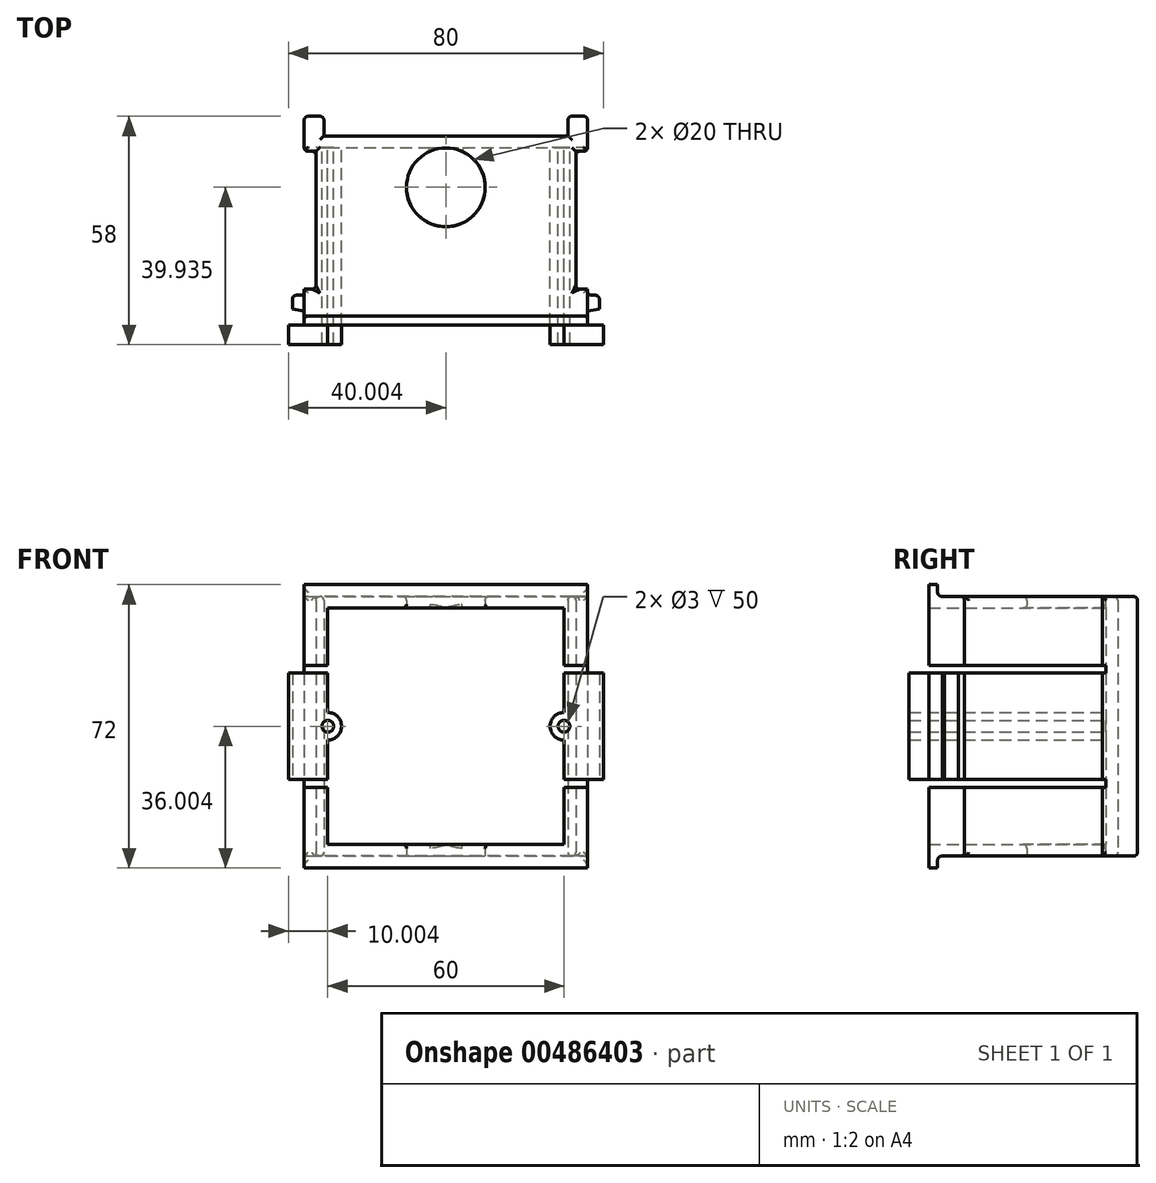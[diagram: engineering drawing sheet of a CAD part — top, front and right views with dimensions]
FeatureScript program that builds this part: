
annotation { "Feature Type Name" : "Feature", "Feature Type Description" : "" }
export const myFeature = defineFeature(function(context is Context, id is Id, definition is map)
    precondition{}
    {
        {
            var Q0;
            Q0=qCreatedBy(makeId("Front.planeOp"),FACE);
            var sketch = newSketch(context, id + "F0", { "sketchPlane" : qUnion([Q0])});
            skLineSegment(sketch, "E0.bottom", {"start": v(-38.09, 40.21) * mm, "end": v(21.91, 40.21) * mm});
            skLineSegment(sketch, "E0.top", {"start": v(-38.09, -19.79) * mm, "end": v(21.91, -19.79) * mm});
            skLineSegment(sketch, "E0.left", {"start": v(-38.09, 40.21) * mm, "end": v(-38.09, 13.71) * mm});
            skLineSegment(sketch, "E0.right", {"start": v(21.91, 40.21) * mm, "end": v(21.91, 13.71) * mm});
            skCircle(sketch, "E1", {"center": v(-38.09, 10.21) * mm, "radius": 1.5 * mm});
            skCircle(sketch, "E2", {"center": v(21.91, 10.21) * mm, "radius": 1.5 * mm});
            skArc(sketch, "E3", {"start": v(-38.09, 6.71) * mm, "mid": v(-34.59, 10.21) * mm, "end": v(-38.09, 13.71) * mm});
            skArc(sketch, "E4", {"start": v(21.91, 13.71) * mm, "mid": v(18.41, 10.21) * mm, "end": v(21.91, 6.71) * mm});
            skLineSegment(sketch, "E5.trimOffspring", {"start": v(-38.09, 6.71) * mm, "end": v(-38.09, -19.79) * mm});
            skLineSegment(sketch, "E6.trimOffspring", {"start": v(21.91, 6.71) * mm, "end": v(21.91, -19.79) * mm});
            skLineSegment(sketch, "E7.bottom", {"start": v(27.91, 46.21) * mm, "end": v(-44.09, 46.21) * mm});
            skLineSegment(sketch, "E7.top", {"start": v(27.91, -25.79) * mm, "end": v(-44.09, -25.79) * mm});
            skLineSegment(sketch, "E7.left", {"start": v(27.91, 46.21) * mm, "end": v(27.91, -25.79) * mm});
            skLineSegment(sketch, "E7.right", {"start": v(-44.09, 46.21) * mm, "end": v(-44.09, -25.79) * mm});
            skPoint(sketch, "E7.middle", {"position": v(-8.09, 10.21) * mm});
            skPoint(sketch, "E7.middle.positionSnap0", {"position": v(18.41, 10.21) * mm});
            skPoint(sketch, "E7.middle.positionSnap1", {"position": v(-8.09, 40.21) * mm});
            skPoint(sketch, "E7.centerSnap0", {"position": v(18.41, 10.21) * mm});
            skPoint(sketch, "E7.centerSnap1", {"position": v(-8.09, 40.21) * mm});
            skSolve(sketch);
        }
        {
            var Q0;
            Q0 = qSketchRegion(id + "F0", true);
            var Q1;
            Q1 = qConstructionFilter(qBodyType(qCreatedBy(id + "F0" ,EDGE), BodyType.WIRE), ConstructionObject.NO);
            extrude(context, id + "F1", {"entities" : qUnion([Q0]), "surfaceEntities" : qUnion([Q1]), "depth" : 45 * mm});
        }
        {
            var Q0;
            Q0=makeQuery(id+"F1.opExtrude","CAP_FACE",FACE,{"disambiguationData":[OSD([sQuery(id+"F0.wireOp",EDGE,"E0.bottom"),sQuery(id+"F0.wireOp",EDGE,"E0.top"),sQuery(id+"F0.wireOp",EDGE,"E0.left"),sQuery(id+"F0.wireOp",EDGE,"E0.right"),sQuery(id+"F0.wireOp",EDGE,"E1"),sQuery(id+"F0.wireOp",EDGE,"E2"),sQuery(id+"F0.wireOp",EDGE,"E3"),sQuery(id+"F0.wireOp",EDGE,"E4"),sQuery(id+"F0.wireOp",EDGE,"E5.trimOffspring"),sQuery(id+"F0.wireOp",EDGE,"E6.trimOffspring"),sQuery(id+"F0.wireOp",EDGE,"E7.bottom"),sQuery(id+"F0.wireOp",EDGE,"E7.top"),sQuery(id+"F0.wireOp",EDGE,"E7.left"),sQuery(id+"F0.wireOp",EDGE,"E7.right")])],"isStart":true});
            var sketch = newSketch(context, id + "F2", { "sketchPlane" : qUnion([Q0])});
            skLineSegment(sketch, "E8.bottom", {"start": v(-27.91, 46.21) * mm, "end": v(44.09, 46.21) * mm});
            skLineSegment(sketch, "E8.top", {"start": v(-27.91, -25.79) * mm, "end": v(44.09, -25.79) * mm});
            skLineSegment(sketch, "E8.left", {"start": v(-27.91, 46.21) * mm, "end": v(-27.91, -25.79) * mm});
            skLineSegment(sketch, "E8.right", {"start": v(44.09, 46.21) * mm, "end": v(44.09, -25.79) * mm});
            skSolve(sketch);
        }
        {
            var Q0;
            Q0 = qSketchRegion(id + "F2", true);
            extrude(context, id + "F3", {"entities" : qUnion([Q0]), "operationType" : NewBodyOperationType.ADD, "depth" : 3 * mm});
        }
        {
            var Q0;
            Q0=makeQuery(id+"F3.opExtrude","CAP_FACE",FACE,{"disambiguationData":[OSD([sQuery(id+"F2.wireOp",EDGE,"E8.bottom"),sQuery(id+"F2.wireOp",EDGE,"E8.top"),sQuery(id+"F2.wireOp",EDGE,"E8.left"),sQuery(id+"F2.wireOp",EDGE,"E8.right")])],"isStart":false});
            var sketch = newSketch(context, id + "F4", { "sketchPlane" : qUnion([Q0])});
            skLineSegment(sketch, "E9.bottom", {"start": v(44.09, 46.21) * mm, "end": v(39.09, 46.21) * mm});
            skLineSegment(sketch, "E9.top", {"start": v(44.09, -25.79) * mm, "end": v(39.09, -25.79) * mm});
            skLineSegment(sketch, "E9.left", {"start": v(44.09, 46.21) * mm, "end": v(44.09, -25.79) * mm});
            skLineSegment(sketch, "E9.right", {"start": v(39.09, 46.21) * mm, "end": v(39.09, -25.79) * mm});
            skLineSegment(sketch, "E10.bottom", {"start": v(-27.91, 46.21) * mm, "end": v(-22.91, 46.21) * mm});
            skLineSegment(sketch, "E10.top", {"start": v(-27.91, -25.79) * mm, "end": v(-22.91, -25.79) * mm});
            skLineSegment(sketch, "E10.left", {"start": v(-27.91, 46.21) * mm, "end": v(-27.91, -25.79) * mm});
            skLineSegment(sketch, "E10.right", {"start": v(-22.91, 46.21) * mm, "end": v(-22.91, -25.79) * mm});
            skSolve(sketch);
        }
        {
            var Q0;
            Q0 = qSketchRegion(id + "F4", true);
            extrude(context, id + "F5", {"entities" : qUnion([Q0]), "operationType" : NewBodyOperationType.ADD, "depth" : 5 * mm});
        }
        {
            var Q0;
            Q0=makeQuery(id+"F1.opExtrude","CAP_FACE",FACE,{"disambiguationData":[OSD([sQuery(id+"F0.wireOp",EDGE,"E0.bottom"),sQuery(id+"F0.wireOp",EDGE,"E0.top"),sQuery(id+"F0.wireOp",EDGE,"E0.left"),sQuery(id+"F0.wireOp",EDGE,"E0.right"),sQuery(id+"F0.wireOp",EDGE,"E1"),sQuery(id+"F0.wireOp",EDGE,"E2"),sQuery(id+"F0.wireOp",EDGE,"E3"),sQuery(id+"F0.wireOp",EDGE,"E4"),sQuery(id+"F0.wireOp",EDGE,"E5.trimOffspring"),sQuery(id+"F0.wireOp",EDGE,"E6.trimOffspring"),sQuery(id+"F0.wireOp",EDGE,"E7.bottom"),sQuery(id+"F0.wireOp",EDGE,"E7.top"),sQuery(id+"F0.wireOp",EDGE,"E7.left"),sQuery(id+"F0.wireOp",EDGE,"E7.right")])],"isStart":false});
            var sketch = newSketch(context, id + "F6", { "sketchPlane" : qUnion([Q0])});
            skLineSegment(sketch, "E11.bottom", {"start": v(-38.09, 23.71) * mm, "end": v(-48.09, 23.71) * mm});
            skLineSegment(sketch, "E11.top", {"start": v(-38.09, -3.29) * mm, "end": v(-48.09, -3.29) * mm});
            skLineSegment(sketch, "E11.left", {"start": v(-38.09, 23.71) * mm, "end": v(-38.09, 13.71) * mm});
            skLineSegment(sketch, "E11.right", {"start": v(-48.09, 23.71) * mm, "end": v(-48.09, -3.29) * mm});
            skArc(sketch, "E12", {"start": v(-38.09, 6.71) * mm, "mid": v(-34.59, 10.21) * mm, "end": v(-38.09, 13.71) * mm});
            skCircle(sketch, "E13", {"center": v(-38.09, 10.21) * mm, "radius": 1.5 * mm});
            skLineSegment(sketch, "E14.trimOffspring", {"start": v(-38.09, 6.71) * mm, "end": v(-38.09, -3.29) * mm});
            skLineSegment(sketch, "E15", {"start": v(-8.09, 40.21) * mm, "end": v(-8.09, -19.79) * mm, "construction": true});
            skLineSegment(sketch, "E16.MirrorCS", {"start": v(21.91, 23.71) * mm, "end": v(31.91, 23.71) * mm});
            skLineSegment(sketch, "E17.MirrorCS", {"start": v(21.91, -3.29) * mm, "end": v(31.91, -3.29) * mm});
            skLineSegment(sketch, "E18.MirrorCS", {"start": v(21.91, 23.71) * mm, "end": v(21.91, 13.71) * mm});
            skLineSegment(sketch, "E19.MirrorCS", {"start": v(21.91, 6.71) * mm, "end": v(21.91, -3.29) * mm});
            skLineSegment(sketch, "E20.MirrorCS", {"start": v(31.91, 23.71) * mm, "end": v(31.91, -3.29) * mm});
            skArc(sketch, "E21.MirrorCS", {"start": v(21.91, 6.71) * mm, "mid": v(18.41, 10.21) * mm, "end": v(21.91, 13.71) * mm});
            skCircle(sketch, "E22.MirrorC", {"center": v(21.91, 10.21) * mm, "radius": 1.5 * mm});
            skSolve(sketch);
        }
        {
            var Q0;
            Q0 = qSketchRegion(id + "F6", true);
            extrude(context, id + "F7", {"entities" : qUnion([Q0]), "operationType" : NewBodyOperationType.ADD, "depth" : 5 * mm});
        }
        {
            var Q0;
            Q0=makeQuery(id+"F5.boolean.opBoolean","MERGE",FACE,{"derivedFrom":[makeQuery(id+"F3.boolean.opBoolean","MERGE",FACE,{"derivedFrom":[makeQuery(id+"F1.opExtrude","SWEPT_FACE",FACE,{"disambiguationData":[OSD([sQuery(id+"F0.wireOp",EDGE,"E7.right")])]}),makeQuery(id+"F3.opExtrude","SWEPT_FACE",FACE,{"disambiguationData":[OSD([sQuery(id+"F2.wireOp",EDGE,"E8.right")])]})]}),makeQuery(id+"F5.opExtrude","SWEPT_FACE",FACE,{"disambiguationData":[OSD([sQuery(id+"F4.wireOp",EDGE,"E9.left")])]})]});
            var sketch = newSketch(context, id + "F8", { "sketchPlane" : qUnion([Q0])});
            skLineSegment(sketch, "E23.bottom", {"start": v(45, 23.71) * mm, "end": v(0, 23.71) * mm});
            skLineSegment(sketch, "E23.top", {"start": v(45, 25.71) * mm, "end": v(0, 25.71) * mm});
            skLineSegment(sketch, "E23.left", {"start": v(45, 23.71) * mm, "end": v(45, 25.71) * mm});
            skLineSegment(sketch, "E23.right", {"start": v(0, 23.71) * mm, "end": v(0, 25.71) * mm});
            skLineSegment(sketch, "E24.bottom", {"start": v(45, -3.29) * mm, "end": v(0, -3.29) * mm});
            skLineSegment(sketch, "E24.top", {"start": v(45, -5.29) * mm, "end": v(0, -5.29) * mm});
            skLineSegment(sketch, "E24.left", {"start": v(45, -3.29) * mm, "end": v(45, -5.29) * mm});
            skLineSegment(sketch, "E24.right", {"start": v(0, -3.29) * mm, "end": v(0, -5.29) * mm});
            skSolve(sketch);
        }
        {
            var Q0;
            Q0 = qSketchRegion(id + "F8", true);
            extrude(context, id + "F9", {"entities" : qUnion([Q0]), "operationType" : NewBodyOperationType.REMOVE, "oppositeDirection" : true, "depth" : 100 * mm});
        }
        {
            var Q0;
            Q0=makeQuery(id+"F9.boolean.opBoolean","MERGE",FACE,{"derivedFrom":[makeQuery(id+"F7.opExtrude","SWEPT_FACE",FACE,{"disambiguationData":[OSD([sQuery(id+"F6.wireOp",EDGE,"E11.top")])]}),makeQuery(id+"F9.opExtrude","SWEPT_FACE",FACE,{"disambiguationData":[OSD([sQuery(id+"F8.wireOp",EDGE,"E24.bottom")])]})]});
            var sketch = newSketch(context, id + "F10", { "sketchPlane" : qUnion([Q0])});
            skLineSegment(sketch, "E25.top", {"start": v(-44.09, 37.5) * mm, "end": v(-47.09, 37.5) * mm});
            skLineSegment(sketch, "E25.left", {"start": v(-44.09, 41.5) * mm, "end": v(-44.09, 37.5) * mm});
            skLineSegment(sketch, "E25.right", {"start": v(-47.09, 40.97) * mm, "end": v(-47.09, 37.5) * mm});
            skLineSegment(sketch, "E26", {"start": v(-44.09, 41.5) * mm, "end": v(-47.09, 40.97) * mm});
            skLineSegment(sketch, "E27", {"start": v(-8.09, 43.31) * mm, "end": v(-8.09, 15.36) * mm, "construction": true});
            skLineSegment(sketch, "E28.MirrorCS", {"start": v(27.91, 41.5) * mm, "end": v(30.91, 40.97) * mm});
            skLineSegment(sketch, "E29.MirrorCS", {"start": v(27.91, 37.5) * mm, "end": v(30.91, 37.5) * mm});
            skLineSegment(sketch, "E30.MirrorCS", {"start": v(30.91, 40.97) * mm, "end": v(30.91, 37.5) * mm});
            skLineSegment(sketch, "E31.MirrorCS", {"start": v(27.91, 41.5) * mm, "end": v(27.91, 37.5) * mm});
            skSolve(sketch);
        }
        {
            var Q0;
            Q0 = qSketchRegion(id + "F10", true);
            extrude(context, id + "F11", {"entities" : qUnion([Q0]), "operationType" : NewBodyOperationType.ADD, "oppositeDirection" : true, "depth" : 27 * mm});
        }
        {
            var Q0;
            {var subQ0=sQuery(id+"F4.wireOp",EDGE,"E10.left");var subQ3=sQuery(id+"F0.wireOp",EDGE,"E7.left");var subQ5=sQuery(id+"F0.wireOp",EDGE,"E7.bottom");var subQ15=sQuery(id+"F2.wireOp",EDGE,"E8.left");var subQ18=makeQuery(id+"F1.opExtrude","SWEPT_FACE",FACE,{"disambiguationData":[OSD([subQ3])]});var subQ19=makeQuery(id+"F3.opExtrude","SWEPT_FACE",FACE,{"disambiguationData":[OSD([subQ15])]});var subQ20=makeQuery(id+"F5.opExtrude","SWEPT_FACE",FACE,{"disambiguationData":[OSD([subQ0])]});Q0=makeQuery(id+"F11.boolean.opBoolean","SPLIT",FACE,{"disambiguationData":[TD([makeQuery(id+"F1.opExtrude","SWEPT_FACE",FACE,{"disambiguationData":[OSD([subQ5])]})])],"derivedFrom":makeQuery(id+"F5.boolean.opBoolean","MERGE",FACE,{"derivedFrom":[makeQuery(id+"F3.boolean.opBoolean","MERGE",FACE,{"derivedFrom":[subQ18,subQ19]}),subQ20]})});}
            var sketch = newSketch(context, id + "F12", { "sketchPlane" : qUnion([Q0])});
            skLineSegment(sketch, "E32", {"start": v(8, 10.21) * mm, "end": v(-53.5, 10.21) * mm, "construction": true});
            skLineSegment(sketch, "E33.bottom", {"start": v(-42.74, 46.21) * mm, "end": v(8, 46.21) * mm});
            skLineSegment(sketch, "E33.top", {"start": v(-42.74, 43.21) * mm, "end": v(8, 43.21) * mm});
            skLineSegment(sketch, "E33.left", {"start": v(-42.74, 46.21) * mm, "end": v(-42.74, 43.21) * mm});
            skLineSegment(sketch, "E33.right", {"start": v(8, 46.21) * mm, "end": v(8, 43.21) * mm});
            skLineSegment(sketch, "E34.MirrorCS", {"start": v(8, -25.79) * mm, "end": v(8, -22.79) * mm});
            skLineSegment(sketch, "E35.MirrorCS", {"start": v(-42.74, -22.79) * mm, "end": v(8, -22.79) * mm});
            skLineSegment(sketch, "E36.MirrorCS", {"start": v(-42.74, -25.79) * mm, "end": v(-42.74, -22.79) * mm});
            skLineSegment(sketch, "E37.MirrorCS", {"start": v(-42.74, -25.79) * mm, "end": v(8, -25.79) * mm});
            skSolve(sketch);
        }
        {
            var Q0;
            Q0 = qSketchRegion(id + "F12", true);
            extrude(context, id + "F13", {"entities" : qUnion([Q0]), "operationType" : NewBodyOperationType.REMOVE, "endBound" : BoundingType.UP_TO_NEXT, "oppositeDirection" : true, "depth" : 25 * mm});
        }
        {
            var Q0;
            Q0=makeQuery(id+"F13.boolean.opBoolean","COPY",FACE,{"derivedFrom":makeQuery(id+"F13.opExtrude","SWEPT_FACE",FACE,{"disambiguationData":[OSD([sQuery(id+"F12.wireOp",EDGE,"E35.MirrorCS")])]})});
            var sketch = newSketch(context, id + "F14", { "sketchPlane" : qUnion([Q0])});
            skLineSegment(sketch, "E38", {"start": v(-8.09, -3) * mm, "end": v(-8.09, 55.12) * mm, "construction": true});
            skLineSegment(sketch, "E39.bottom", {"start": v(27.91, 35.92) * mm, "end": v(24.91, 35.92) * mm});
            skLineSegment(sketch, "E39.top", {"start": v(27.91, 0.92) * mm, "end": v(24.91, 0.92) * mm});
            skLineSegment(sketch, "E39.left", {"start": v(27.91, 35.92) * mm, "end": v(27.91, 0.92) * mm});
            skLineSegment(sketch, "E39.right", {"start": v(24.91, 35.92) * mm, "end": v(24.91, 0.92) * mm});
            skLineSegment(sketch, "E40.MirrorCS", {"start": v(-44.09, 0.92) * mm, "end": v(-41.09, 0.92) * mm});
            skLineSegment(sketch, "E41.MirrorCS", {"start": v(-44.09, 35.92) * mm, "end": v(-41.09, 35.92) * mm});
            skLineSegment(sketch, "E42.MirrorCS", {"start": v(-41.09, 35.92) * mm, "end": v(-41.09, 0.92) * mm});
            skLineSegment(sketch, "E43.MirrorCS", {"start": v(-44.09, 35.92) * mm, "end": v(-44.09, 0.92) * mm});
            skSolve(sketch);
        }
        {
            var Q0;
            Q0 = qSketchRegion(id + "F14", true);
            extrude(context, id + "F15", {"entities" : qUnion([Q0]), "operationType" : NewBodyOperationType.REMOVE, "endBound" : BoundingType.THROUGH_ALL, "oppositeDirection" : true, "depth" : 25 * mm});
        }
        {
            var Q0;
            Q0=makeQuery(id+"F13.boolean.opBoolean","COPY",FACE,{"derivedFrom":makeQuery(id+"F13.opExtrude","SWEPT_FACE",FACE,{"disambiguationData":[OSD([sQuery(id+"F12.wireOp",EDGE,"E35.MirrorCS")])]})});
            var Q1;
            Q1=makeQuery(id+"F13.boolean.opBoolean","COPY",FACE,{"derivedFrom":makeQuery(id+"F13.opExtrude","SWEPT_FACE",FACE,{"disambiguationData":[OSD([sQuery(id+"F12.wireOp",EDGE,"E33.top")])]})});
            fillet(context, id + "F16", {"entities" : qUnion([Q0, Q1]), "radius" : 1 * mm, "tangentPropagation" : true, "allowEdgeOverflow" : false});
        }
        {
            var Q0;
            {var subQ0=sQuery(id+"F14.wireOp",EDGE,"E39.bottom");var subQ5=sQuery(id+"F14.wireOp",EDGE,"E39.right");Q0=makeQuery(id+"F15.boolean.opBoolean","COPY",EDGE,{"disambiguationData":[TD([makeQuery(id+"F7.opExtrude","SWEPT_FACE",FACE,{"disambiguationData":[OSD([sQuery(id+"F6.wireOp",EDGE,"E16.MirrorCS")])]})])],"derivedFrom":makeQuery(id+"F15.opExtrude","SWEPT_EDGE",EDGE,{"disambiguationData":[OSD([subQ0,subQ5])]})});}
            var Q1;
            Q1=makeQuery(id+"F11.opExtrude","SWEPT_EDGE",EDGE,{"disambiguationData":[OSD([sQuery(id+"F10.wireOp",EDGE,"E29.MirrorCS"),sQuery(id+"F10.wireOp",EDGE,"E31.MirrorCS")])]});
            var Q2;
            Q2=makeQuery(id+"F11.opExtrude","SWEPT_EDGE",EDGE,{"disambiguationData":[OSD([sQuery(id+"F10.wireOp",EDGE,"E29.MirrorCS"),sQuery(id+"F10.wireOp",EDGE,"E30.MirrorCS")])]});
            var Q3;
            Q3=makeQuery(id+"F11.opExtrude","SWEPT_EDGE",EDGE,{"disambiguationData":[OSD([sQuery(id+"F10.wireOp",EDGE,"E25.top"),sQuery(id+"F10.wireOp",EDGE,"E25.right")])]});
            var Q4;
            {var subQ4=sQuery(id+"F4.wireOp",EDGE,"E9.left");var subQ5=sQuery(id+"F2.wireOp",EDGE,"E8.right");var subQ6=sQuery(id+"F0.wireOp",EDGE,"E7.right");var subQ7=sQuery(id+"F14.wireOp",EDGE,"E41.MirrorCS");Q4=makeQuery(id+"F15.boolean.opBoolean","COPY",EDGE,{"disambiguationData":[TD([makeQuery(id+"F7.opExtrude","SWEPT_FACE",FACE,{"disambiguationData":[OSD([sQuery(id+"F6.wireOp",EDGE,"E11.bottom")])]})])],"derivedFrom":makeQuery(id+"F15.opExtrude","SWEPT_EDGE",EDGE,{"disambiguationData":[OSD([subQ6,subQ5,subQ4,sQuery(id+"F12.wireOp",EDGE,"E35.MirrorCS"),subQ7,sQuery(id+"F14.wireOp",EDGE,"E43.MirrorCS")])]})});}
            var Q5;
            {var subQ4=sQuery(id+"F14.wireOp",EDGE,"E41.MirrorCS");var subQ5=sQuery(id+"F14.wireOp",EDGE,"E42.MirrorCS");Q5=makeQuery(id+"F15.boolean.opBoolean","COPY",EDGE,{"disambiguationData":[TD([makeQuery(id+"F7.opExtrude","SWEPT_FACE",FACE,{"disambiguationData":[OSD([sQuery(id+"F6.wireOp",EDGE,"E11.bottom")])]})])],"derivedFrom":makeQuery(id+"F15.opExtrude","SWEPT_EDGE",EDGE,{"disambiguationData":[OSD([subQ4,subQ5])]})});}
            fillet(context, id + "F17", {"entities" : qUnion([Q0, Q1, Q2, Q3, Q4, Q5]), "radius" : 1 * mm, "tangentPropagation" : true, "allowEdgeOverflow" : false});
        }
        {
            var Q0;
            Q0=makeQuery(id+"F11.opExtrude","SWEPT_EDGE",EDGE,{"disambiguationData":[OSD([sQuery(id+"F8.wireOp",EDGE,"E24.bottom"),sQuery(id+"F10.wireOp",EDGE,"E25.top"),sQuery(id+"F10.wireOp",EDGE,"E25.left")])]});
            var Q1;
            {var subQ4=sQuery(id+"F14.wireOp",EDGE,"E40.MirrorCS");var subQ5=sQuery(id+"F14.wireOp",EDGE,"E42.MirrorCS");Q1=makeQuery(id+"F15.boolean.opBoolean","COPY",EDGE,{"disambiguationData":[TD([makeQuery(id+"F7.opExtrude","SWEPT_FACE",FACE,{"disambiguationData":[OSD([sQuery(id+"F6.wireOp",EDGE,"E11.bottom")])]})])],"derivedFrom":makeQuery(id+"F15.opExtrude","SWEPT_EDGE",EDGE,{"disambiguationData":[OSD([subQ4,subQ5])]})});}
            var Q2;
            {var subQ4=sQuery(id+"F4.wireOp",EDGE,"E9.left");var subQ5=sQuery(id+"F2.wireOp",EDGE,"E8.right");var subQ6=sQuery(id+"F0.wireOp",EDGE,"E7.right");var subQ7=sQuery(id+"F14.wireOp",EDGE,"E40.MirrorCS");Q2=makeQuery(id+"F15.boolean.opBoolean","COPY",EDGE,{"disambiguationData":[TD([makeQuery(id+"F7.opExtrude","SWEPT_FACE",FACE,{"disambiguationData":[OSD([sQuery(id+"F6.wireOp",EDGE,"E11.bottom")])]})])],"derivedFrom":makeQuery(id+"F15.opExtrude","SWEPT_EDGE",EDGE,{"disambiguationData":[OSD([subQ6,subQ5,subQ4,sQuery(id+"F12.wireOp",EDGE,"E35.MirrorCS"),subQ7,sQuery(id+"F14.wireOp",EDGE,"E43.MirrorCS")])]})});}
            var Q3;
            {var subQ0=sQuery(id+"F14.wireOp",EDGE,"E39.bottom");Q3=makeQuery(id+"F15.boolean.opBoolean","COPY",EDGE,{"disambiguationData":[TD([makeQuery(id+"F7.opExtrude","SWEPT_FACE",FACE,{"disambiguationData":[OSD([sQuery(id+"F6.wireOp",EDGE,"E16.MirrorCS")])]})])],"derivedFrom":makeQuery(id+"F15.opExtrude","SWEPT_EDGE",EDGE,{"disambiguationData":[OSD([sQuery(id+"F12.wireOp",EDGE,"E35.MirrorCS"),subQ0,sQuery(id+"F14.wireOp",EDGE,"E39.left")])]})});}
            var Q4;
            {var subQ0=sQuery(id+"F14.wireOp",EDGE,"E39.top");var subQ5=sQuery(id+"F14.wireOp",EDGE,"E39.right");Q4=makeQuery(id+"F15.boolean.opBoolean","COPY",EDGE,{"disambiguationData":[TD([makeQuery(id+"F7.opExtrude","SWEPT_FACE",FACE,{"disambiguationData":[OSD([sQuery(id+"F6.wireOp",EDGE,"E16.MirrorCS")])]})])],"derivedFrom":makeQuery(id+"F15.opExtrude","SWEPT_EDGE",EDGE,{"disambiguationData":[OSD([subQ0,subQ5])]})});}
            var Q5;
            {var subQ0=sQuery(id+"F14.wireOp",EDGE,"E39.top");Q5=makeQuery(id+"F15.boolean.opBoolean","COPY",EDGE,{"disambiguationData":[TD([makeQuery(id+"F7.opExtrude","SWEPT_FACE",FACE,{"disambiguationData":[OSD([sQuery(id+"F6.wireOp",EDGE,"E16.MirrorCS")])]})])],"derivedFrom":makeQuery(id+"F15.opExtrude","SWEPT_EDGE",EDGE,{"disambiguationData":[OSD([sQuery(id+"F12.wireOp",EDGE,"E35.MirrorCS"),subQ0,sQuery(id+"F14.wireOp",EDGE,"E39.left")])]})});}
            fillet(context, id + "F18", {"entities" : qUnion([Q0, Q1, Q2, Q3, Q4, Q5]), "radius" : 1 * mm, "tangentPropagation" : true, "allowEdgeOverflow" : false});
        }
        {
            var Q0;
            {var subQ6=sQuery(id+"F14.wireOp",EDGE,"E39.bottom");Q0=makeQuery(id+"F15.boolean.opBoolean","COPY",EDGE,{"disambiguationData":[TD([makeQuery(id+"F13.boolean.opBoolean","COPY",FACE,{"derivedFrom":makeQuery(id+"F13.opExtrude","SWEPT_FACE",FACE,{"disambiguationData":[OSD([sQuery(id+"F12.wireOp",EDGE,"E33.top")])]})})])],"derivedFrom":makeQuery(id+"F15.opExtrude","SWEPT_EDGE",EDGE,{"disambiguationData":[OSD([sQuery(id+"F12.wireOp",EDGE,"E35.MirrorCS"),subQ6,sQuery(id+"F14.wireOp",EDGE,"E39.left")])]})});}
            var Q1;
            {var subQ3=sQuery(id+"F14.wireOp",EDGE,"E39.bottom");var subQ4=sQuery(id+"F14.wireOp",EDGE,"E39.right");Q1=makeQuery(id+"F15.boolean.opBoolean","COPY",EDGE,{"disambiguationData":[TD([makeQuery(id+"F13.boolean.opBoolean","COPY",FACE,{"derivedFrom":makeQuery(id+"F13.opExtrude","SWEPT_FACE",FACE,{"disambiguationData":[OSD([sQuery(id+"F12.wireOp",EDGE,"E33.top")])]})})])],"derivedFrom":makeQuery(id+"F15.opExtrude","SWEPT_EDGE",EDGE,{"disambiguationData":[OSD([subQ3,subQ4])]})});}
            var Q2;
            {var subQ6=sQuery(id+"F12.wireOp",EDGE,"E35.MirrorCS");var subQ7=sQuery(id+"F14.wireOp",EDGE,"E39.bottom");Q2=makeQuery(id+"F15.boolean.opBoolean","COPY",EDGE,{"disambiguationData":[TD([makeQuery(id+"F13.boolean.opBoolean","COPY",FACE,{"derivedFrom":makeQuery(id+"F13.opExtrude","SWEPT_FACE",FACE,{"disambiguationData":[OSD([subQ6])]})})])],"derivedFrom":makeQuery(id+"F15.opExtrude","SWEPT_EDGE",EDGE,{"disambiguationData":[OSD([subQ6,subQ7,sQuery(id+"F14.wireOp",EDGE,"E39.left")])]})});}
            var Q3;
            {var subQ3=sQuery(id+"F14.wireOp",EDGE,"E39.bottom");var subQ4=sQuery(id+"F14.wireOp",EDGE,"E39.right");Q3=makeQuery(id+"F15.boolean.opBoolean","COPY",EDGE,{"disambiguationData":[TD([makeQuery(id+"F13.boolean.opBoolean","COPY",FACE,{"derivedFrom":makeQuery(id+"F13.opExtrude","SWEPT_FACE",FACE,{"disambiguationData":[OSD([sQuery(id+"F12.wireOp",EDGE,"E35.MirrorCS")])]})})])],"derivedFrom":makeQuery(id+"F15.opExtrude","SWEPT_EDGE",EDGE,{"disambiguationData":[OSD([subQ3,subQ4])]})});}
            var Q4;
            {var subQ3=sQuery(id+"F14.wireOp",EDGE,"E41.MirrorCS");var subQ4=sQuery(id+"F14.wireOp",EDGE,"E42.MirrorCS");Q4=makeQuery(id+"F15.boolean.opBoolean","COPY",EDGE,{"disambiguationData":[TD([makeQuery(id+"F13.boolean.opBoolean","COPY",FACE,{"derivedFrom":makeQuery(id+"F13.opExtrude","SWEPT_FACE",FACE,{"disambiguationData":[OSD([sQuery(id+"F12.wireOp",EDGE,"E33.top")])]})})])],"derivedFrom":makeQuery(id+"F15.opExtrude","SWEPT_EDGE",EDGE,{"disambiguationData":[OSD([subQ3,subQ4])]})});}
            var Q5;
            {var subQ0=sQuery(id+"F4.wireOp",EDGE,"E9.left");var subQ2=sQuery(id+"F0.wireOp",EDGE,"E7.right");var subQ5=sQuery(id+"F2.wireOp",EDGE,"E8.right");var subQ7=sQuery(id+"F14.wireOp",EDGE,"E41.MirrorCS");Q5=makeQuery(id+"F15.boolean.opBoolean","COPY",EDGE,{"disambiguationData":[TD([makeQuery(id+"F13.boolean.opBoolean","COPY",FACE,{"derivedFrom":makeQuery(id+"F13.opExtrude","SWEPT_FACE",FACE,{"disambiguationData":[OSD([sQuery(id+"F12.wireOp",EDGE,"E33.top")])]})})])],"derivedFrom":makeQuery(id+"F15.opExtrude","SWEPT_EDGE",EDGE,{"disambiguationData":[OSD([subQ2,subQ5,subQ0,sQuery(id+"F12.wireOp",EDGE,"E35.MirrorCS"),subQ7,sQuery(id+"F14.wireOp",EDGE,"E43.MirrorCS")])]})});}
            var Q6;
            {var subQ3=sQuery(id+"F14.wireOp",EDGE,"E41.MirrorCS");var subQ4=sQuery(id+"F14.wireOp",EDGE,"E42.MirrorCS");Q6=makeQuery(id+"F15.boolean.opBoolean","COPY",EDGE,{"disambiguationData":[TD([makeQuery(id+"F13.boolean.opBoolean","COPY",FACE,{"derivedFrom":makeQuery(id+"F13.opExtrude","SWEPT_FACE",FACE,{"disambiguationData":[OSD([sQuery(id+"F12.wireOp",EDGE,"E35.MirrorCS")])]})})])],"derivedFrom":makeQuery(id+"F15.opExtrude","SWEPT_EDGE",EDGE,{"disambiguationData":[OSD([subQ3,subQ4])]})});}
            var Q7;
            {var subQ0=sQuery(id+"F4.wireOp",EDGE,"E9.left");var subQ2=sQuery(id+"F12.wireOp",EDGE,"E35.MirrorCS");var subQ3=sQuery(id+"F2.wireOp",EDGE,"E8.right");var subQ5=sQuery(id+"F0.wireOp",EDGE,"E7.right");var subQ8=sQuery(id+"F14.wireOp",EDGE,"E41.MirrorCS");Q7=makeQuery(id+"F15.boolean.opBoolean","COPY",EDGE,{"disambiguationData":[TD([makeQuery(id+"F13.boolean.opBoolean","COPY",FACE,{"derivedFrom":makeQuery(id+"F13.opExtrude","SWEPT_FACE",FACE,{"disambiguationData":[OSD([subQ2])]})})])],"derivedFrom":makeQuery(id+"F15.opExtrude","SWEPT_EDGE",EDGE,{"disambiguationData":[OSD([subQ5,subQ3,subQ0,subQ2,subQ8,sQuery(id+"F14.wireOp",EDGE,"E43.MirrorCS")])]})});}
            var Q8;
            Q8=makeQuery(id+"F5.opExtrude","CAP_EDGE",EDGE,{"disambiguationData":[OSD([sQuery(id+"F4.wireOp",EDGE,"E9.left")])],"isStart":false});
            var Q9;
            Q9=makeQuery(id+"F5.opExtrude","CAP_EDGE",EDGE,{"disambiguationData":[OSD([sQuery(id+"F4.wireOp",EDGE,"E9.right")])],"isStart":false});
            var Q10;
            Q10=makeQuery(id+"F5.opExtrude","CAP_EDGE",EDGE,{"disambiguationData":[OSD([sQuery(id+"F4.wireOp",EDGE,"E10.right")])],"isStart":false});
            var Q11;
            Q11=makeQuery(id+"F5.opExtrude","CAP_EDGE",EDGE,{"disambiguationData":[OSD([sQuery(id+"F4.wireOp",EDGE,"E10.left")])],"isStart":false});
            fillet(context, id + "F19", {"entities" : qUnion([Q0, Q1, Q2, Q3, Q4, Q5, Q6, Q7, Q8, Q9, Q10, Q11]), "radius" : 1 * mm, "tangentPropagation" : true, "allowEdgeOverflow" : false});
        }
        {
            var Q0;
            Q0=makeQuery(id+"F13.boolean.opBoolean","COPY",FACE,{"derivedFrom":makeQuery(id+"F13.opExtrude","SWEPT_FACE",FACE,{"disambiguationData":[OSD([sQuery(id+"F12.wireOp",EDGE,"E35.MirrorCS")])]})});
            var sketch = newSketch(context, id + "F20", { "sketchPlane" : qUnion([Q0])});
            skLineSegment(sketch, "E44", {"start": v(-8.09, -2) * mm, "end": v(-8.09, 55.18) * mm, "construction": true});
            skLineSegment(sketch, "E45", {"start": v(51.01, 10.06) * mm, "end": v(-54.94, 10.06) * mm, "construction": true});
            skCircle(sketch, "E46", {"center": v(-8.09, 10.06) * mm, "radius": 10 * mm});
            skSolve(sketch);
        }
        {
            var Q0;
            Q0 = qSketchRegion(id + "F20", true);
            extrude(context, id + "F21", {"entities" : qUnion([Q0]), "operationType" : NewBodyOperationType.REMOVE, "endBound" : BoundingType.THROUGH_ALL, "oppositeDirection" : true, "depth" : 25 * mm});
        }
        {
            var Q0;
            Q0=makeQuery(id+"F21.boolean.opBoolean","COPY",EDGE,{"derivedFrom":makeQuery(id+"F21.opExtrude","CAP_EDGE",EDGE,{"disambiguationData":[OSD([sQuery(id+"F20.wireOp",EDGE,"E46")])],"isStart":true})});
            var Q1;
            Q1=makeQuery(id+"F21.boolean.opBoolean","INTERSECT",EDGE,{"derivedFrom":[makeQuery(id+"F1.opExtrude","SWEPT_FACE",FACE,{"disambiguationData":[OSD([sQuery(id+"F0.wireOp",EDGE,"E0.top")])]}),makeQuery(id+"F21.opExtrude","SWEPT_FACE",FACE,{"disambiguationData":[OSD([sQuery(id+"F20.wireOp",EDGE,"E46")])]})]});
            var Q2;
            Q2=makeQuery(id+"F21.boolean.opBoolean","INTERSECT",EDGE,{"derivedFrom":[makeQuery(id+"F1.opExtrude","SWEPT_FACE",FACE,{"disambiguationData":[OSD([sQuery(id+"F0.wireOp",EDGE,"E0.bottom")])]}),makeQuery(id+"F21.opExtrude","SWEPT_FACE",FACE,{"disambiguationData":[OSD([sQuery(id+"F20.wireOp",EDGE,"E46")])]})]});
            var Q3;
            Q3=makeQuery(id+"F21.boolean.opBoolean","INTERSECT",EDGE,{"derivedFrom":[makeQuery(id+"F13.boolean.opBoolean","COPY",FACE,{"derivedFrom":makeQuery(id+"F13.opExtrude","SWEPT_FACE",FACE,{"disambiguationData":[OSD([sQuery(id+"F12.wireOp",EDGE,"E33.top")])]})}),makeQuery(id+"F21.opExtrude","SWEPT_FACE",FACE,{"disambiguationData":[OSD([sQuery(id+"F20.wireOp",EDGE,"E46")])]})]});
            fillet(context, id + "F22", {"entities" : qUnion([Q0, Q1, Q2, Q3]), "radius" : 1 * mm, "tangentPropagation" : true, "allowEdgeOverflow" : false});
        }
    });
